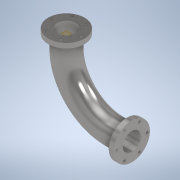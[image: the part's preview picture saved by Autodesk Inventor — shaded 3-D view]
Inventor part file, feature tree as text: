
AUTODESK INVENTOR PART (.ipt)
format: ipt  version: 2022 (Build 260153000, 153)  size: 205,824 bytes
history: native  units: mm
features: sketch x4, extrude x2, plane x1, sweep x1
ambient origin geometry x8: Origin, YZ Plane, XZ Plane, XY Plane, X Axis, Y Axis, Z Axis, Center Point
bodies: Body1 (feature_tree)
feature tree (8):
  sketch  "Sketch1"  dims[d3=150.0mm d4=75.0mm]
  plane  "Work Plane1"
  sketch  "Sketch2"  dims[d5=10.0mm d6=62.5mm]
  sweep  "Sweep2"
  extrude  "Extrusion3"  Depth=10.0mm
  extrude  "Extrusion4"  Depth=100.0mm
  sketch  "Sketch3"  dims[d7=60.0mm d9=360.0deg d11=100.0mm]
  sketch  "Sketch5"  dims[d12=75.0mm d30=400.0mm d31=50.0mm d32=50.0mm d33=0.0mm d34=0.0mm d35=20.0mm d36=0.0mm d38=60.0mm d39=150.0mm d40=75.0mm d41=10.0mm d42=62.5mm d43=360.0deg d48=20.0mm d49=0.0mm]
